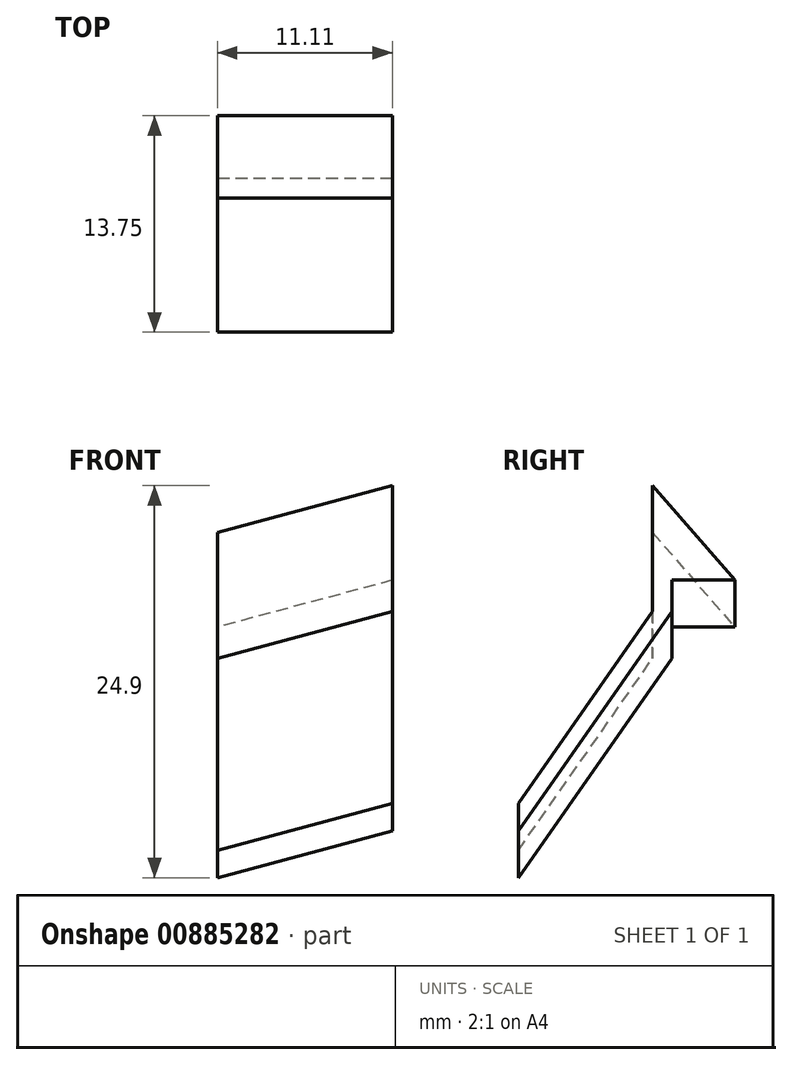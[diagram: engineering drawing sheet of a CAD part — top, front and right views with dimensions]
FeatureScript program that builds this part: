
annotation { "Feature Type Name" : "Feature", "Feature Type Description" : "" }
export const myFeature = defineFeature(function(context is Context, id is Id, definition is map)
    precondition{}
    {
        {
            var Q0;
            Q0=qCreatedBy(makeId("Right.planeOp"),FACE);
            var sketch = newSketch(context, id + "F0", { "sketchPlane" : qUnion([Q0])});
            skLineSegment(sketch, "E0", {"start": v(0, 0) * mm, "end": v(0, -15) * mm, "construction": true});
            skLineSegment(sketch, "E1", {"start": v(0, 0) * mm, "end": v(-9.75, -13.93) * mm});
            skLineSegment(sketch, "E2", {"start": v(-9.75, -13.93) * mm, "end": v(-9.75, -12.18) * mm});
            skLineSegment(sketch, "E3", {"start": v(-9.75, -12.18) * mm, "end": v(-1.22, 0) * mm});
            skLineSegment(sketch, "E4", {"start": v(0, 0) * mm, "end": v(0, 2) * mm});
            skLineSegment(sketch, "E5", {"start": v(0, 2) * mm, "end": v(4, 2) * mm});
            skLineSegment(sketch, "E6", {"start": v(-1.22, 8) * mm, "end": v(4, 2) * mm});
            skLineSegment(sketch, "E7", {"start": v(-1.22, 0) * mm, "end": v(-1.22, 2) * mm});
            skLineSegment(sketch, "E8", {"start": v(-1.22, 2) * mm, "end": v(-1.22, 8) * mm});
            skSolve(sketch);
        }
        {
            var Q0;
            Q0=sQuery(id+"F0.wireOp",EDGE,"E8");
            cPlane(context, id + "F1", {"entities" : qUnion([Q0]), "cplaneType" : CPlaneType.LINE_ANGLE, "offset" : 25 * mm, "angle" : 90 * degree, "width" : 150 * mm, "height" : 150 * mm});
        }
        {
            var Q0;
            Q0=qCreatedBy(id+"F1.planeOp",FACE);
            var sketch = newSketch(context, id + "F2", { "sketchPlane" : qUnion([Q0])});
            skPoint(sketch, "E9.0", {"position": v(0, 8) * mm});
            skLineSegment(sketch, "E10.0", {"start": v(0, 2) * mm, "end": v(0, 8) * mm});
            skLineSegment(sketch, "E11", {"start": v(0, 8) * mm, "end": v(11.1, 5.02) * mm});
            skSolve(sketch);
        }
        {
            var Q0;
            Q0=makeQuery(id+"F0.imprint","IMPRINT",FACE,{"disambiguationData":[TD([[makeQuery(id+"F0.imprint","IMPRINT",EDGE,{"derivedFrom":sQuery(id+"F0.wireOp",EDGE,"E1")}),-1.0]])]});
            var Q1;
            Q1=sQuery(id+"F2.wireOp",EDGE,"E11");
            sweep(context, id + "F3", {"profiles" : qUnion([Q0]), "path" : qUnion([Q1])});
        }
    });
